FCSTD DOCUMENT  (FreeCAD 0.19R14555 (Git shallow))
Label: dfsdfd
License: All rights reserved
LicenseURL: http://en.wikipedia.org/wiki/All_rights_reserved
objects: Sketcher::SketchObject×1, PartDesign::Body×1
note: 2 computed .brp shape members not serialized (recipe doc carries the construction recipe); baked Part::Feature solids carry a one-line shape summary decoded from their .brp

FEATURE [Sketcher::SketchObject] Sketch
  FullyConstrained = false
  MapMode = 5
  Support = -> [XY_Plane]
  sketch-geometry (98):
    g0: LineSegment StartX=-62.5 StartY=60 StartZ=0 EndX=62.5 EndY=60 EndZ=0
    g1: LineSegment StartX=62.5 StartY=60 StartZ=0 EndX=62.5 EndY=0 EndZ=0
    g2: LineSegment StartX=62.5 StartY=0 StartZ=0 EndX=-62.5 EndY=0 EndZ=0
    g3: LineSegment StartX=-62.5 StartY=0 StartZ=0 EndX=-62.5 EndY=60 EndZ=0
    g4: LineSegment StartX=-82.5 StartY=25 StartZ=0 EndX=-127.5 EndY=25 EndZ=0
    g5: LineSegment StartX=-127.5 StartY=25 StartZ=0 EndX=-127.5 EndY=0 EndZ=0
    g6: LineSegment StartX=-127.5 StartY=0 StartZ=0 EndX=-82.5 EndY=0 EndZ=0
    g7: LineSegment StartX=-82.5 StartY=0 StartZ=0 EndX=-82.5 EndY=25 EndZ=0
    g8: LineSegment StartX=-147.5 StartY=25 StartZ=0 EndX=-192.5 EndY=25 EndZ=0
    g9: LineSegment StartX=-192.5 StartY=25 StartZ=0 EndX=-192.5 EndY=0 EndZ=0
    g10: LineSegment StartX=-192.5 StartY=0 StartZ=0 EndX=-147.5 EndY=0 EndZ=0
    g11: LineSegment StartX=-147.5 StartY=0 StartZ=0 EndX=-147.5 EndY=25 EndZ=0
    g12: LineSegment StartX=-62.5 StartY=35 StartZ=0 EndX=-200 EndY=35 EndZ=0
    g13: LineSegment StartX=-200 StartY=35 StartZ=0 EndX=-220.856 EndY=17.5 EndZ=0
    g14: LineSegment StartX=-220.856 StartY=17.5 StartZ=0 EndX=-200 EndY=0 EndZ=0
    g15: LineSegment StartX=-200 StartY=0 StartZ=0 EndX=-220.856 EndY=-17.5 EndZ=0
    g16: LineSegment StartX=-220.856 StartY=-17.5 StartZ=0 EndX=-200 EndY=-35 EndZ=0
    g17: LineSegment StartX=-200 StartY=-35 StartZ=0 EndX=0 EndY=-35 EndZ=0
    g18: LineSegment StartX=-192.5 StartY=-10 StartZ=0 EndX=-147.5 EndY=-10 EndZ=0
    g19: LineSegment StartX=-147.5 StartY=-10 StartZ=0 EndX=-147.5 EndY=-35 EndZ=0
    g20: LineSegment StartX=-147.5 StartY=-35 StartZ=0 EndX=-192.5 EndY=-35 EndZ=0
    g21: LineSegment StartX=-192.5 StartY=-35 StartZ=0 EndX=-192.5 EndY=-10 EndZ=0
    g22: LineSegment StartX=-127.5 StartY=-10 StartZ=0 EndX=-82.5 EndY=-10 EndZ=0
    g23: LineSegment StartX=-82.5 StartY=-10 StartZ=0 EndX=-82.5 EndY=-35 EndZ=0
    g24: LineSegment StartX=-82.5 StartY=-35 StartZ=0 EndX=-127.5 EndY=-35 EndZ=0
    g25: LineSegment StartX=-127.5 StartY=-35 StartZ=0 EndX=-127.5 EndY=-10 EndZ=0
    g26: LineSegment StartX=-192.5 StartY=60 StartZ=0 EndX=-147.5 EndY=60 EndZ=0
    g27: LineSegment StartX=-147.5 StartY=60 StartZ=0 EndX=-147.5 EndY=35 EndZ=0
    g28: LineSegment StartX=-147.5 StartY=35 StartZ=0 EndX=-192.5 EndY=35 EndZ=0
    g29: LineSegment StartX=-192.5 StartY=35 StartZ=0 EndX=-192.5 EndY=60 EndZ=0
    g30: LineSegment StartX=-127.5 StartY=60 StartZ=0 EndX=-82.5 EndY=60 EndZ=0
    g31: LineSegment StartX=-82.5 StartY=60 StartZ=0 EndX=-82.5 EndY=35 EndZ=0
    g32: LineSegment StartX=-82.5 StartY=35 StartZ=0 EndX=-127.5 EndY=35 EndZ=0
    g33: LineSegment StartX=-127.5 StartY=35 StartZ=0 EndX=-127.5 EndY=60 EndZ=0
    g34: LineSegment StartX=-4.5 StartY=12 StartZ=0 EndX=4.5 EndY=12 EndZ=0
    g35: LineSegment StartX=4.5 StartY=12 StartZ=0 EndX=4.5 EndY=0 EndZ=0
    g36: LineSegment StartX=4.5 StartY=0 StartZ=0 EndX=-4.5 EndY=0 EndZ=0
    g37: LineSegment StartX=-4.5 StartY=0 StartZ=0 EndX=-4.5 EndY=12 EndZ=0
    g38: LineSegment StartX=-4.5 StartY=-23 StartZ=0 EndX=4.5 EndY=-23 EndZ=0
    g39: LineSegment StartX=4.5 StartY=-23 StartZ=0 EndX=4.5 EndY=-35 EndZ=0
    g40: LineSegment StartX=4.5 StartY=-35 StartZ=0 EndX=-4.5 EndY=-35 EndZ=0
    g41: LineSegment StartX=-4.5 StartY=-35 StartZ=0 EndX=-4.5 EndY=-23 EndZ=0
    g42: LineSegment StartX=-62.5 StartY=-10 StartZ=0 EndX=-17.5 EndY=-10 EndZ=0
    g43: LineSegment StartX=-17.5 StartY=-10 StartZ=0 EndX=-17.5 EndY=-35 EndZ=0
    g44: LineSegment StartX=-17.5 StartY=-35 StartZ=0 EndX=-62.5 EndY=-35 EndZ=0
    g45: LineSegment StartX=-62.5 StartY=-35 StartZ=0 EndX=-62.5 EndY=-10 EndZ=0
    g46: LineSegment StartX=-200 StartY=0 StartZ=0 EndX=-62.5 EndY=0 EndZ=0
    g47: LineSegment StartX=-62.5 StartY=35 StartZ=0 EndX=62.5 EndY=35 EndZ=0
    g48: LineSegment StartX=-17.5 StartY=0 StartZ=0 EndX=-52.5 EndY=35 EndZ=0
    g49: LineSegment StartX=62.5 StartY=60 StartZ=0 EndX=-62.5 EndY=60 EndZ=0
    g50: LineSegment StartX=-62.5 StartY=60 StartZ=0 EndX=-62.5 EndY=0 EndZ=0
    g51: LineSegment StartX=-62.5 StartY=0 StartZ=0 EndX=62.5 EndY=0 EndZ=0
    g52: LineSegment StartX=62.5 StartY=0 StartZ=0 EndX=62.5 EndY=60 EndZ=0
    g53: LineSegment StartX=82.5 StartY=25 StartZ=0 EndX=127.5 EndY=25 EndZ=0
    g54: LineSegment StartX=127.5 StartY=25 StartZ=0 EndX=127.5 EndY=0 EndZ=0
    g55: LineSegment StartX=127.5 StartY=0 StartZ=0 EndX=82.5 EndY=0 EndZ=0
    g56: LineSegment StartX=82.5 StartY=0 StartZ=0 EndX=82.5 EndY=25 EndZ=0
    g57: LineSegment StartX=147.5 StartY=25 StartZ=0 EndX=192.5 EndY=25 EndZ=0
    g58: LineSegment StartX=192.5 StartY=25 StartZ=0 EndX=192.5 EndY=0 EndZ=0
    g59: LineSegment StartX=192.5 StartY=0 StartZ=0 EndX=147.5 EndY=0 EndZ=0
    g60: LineSegment StartX=147.5 StartY=0 StartZ=0 EndX=147.5 EndY=25 EndZ=0
    g61: LineSegment StartX=62.5 StartY=35 StartZ=0 EndX=200 EndY=35 EndZ=0
    g62: LineSegment StartX=200 StartY=35 StartZ=0 EndX=220.856 EndY=17.5 EndZ=0
    g63: LineSegment StartX=220.856 StartY=17.5 StartZ=0 EndX=200 EndY=0 EndZ=0
    g64: LineSegment StartX=200 StartY=0 StartZ=0 EndX=220.856 EndY=-17.5 EndZ=0
    g65: LineSegment StartX=220.856 StartY=-17.5 StartZ=0 EndX=200 EndY=-35 EndZ=0
    g66: LineSegment StartX=200 StartY=-35 StartZ=0 EndX=0 EndY=-35 EndZ=0
    g67: LineSegment StartX=192.5 StartY=-10 StartZ=0 EndX=147.5 EndY=-10 EndZ=0
    g68: LineSegment StartX=147.5 StartY=-10 StartZ=0 EndX=147.5 EndY=-35 EndZ=0
    g69: LineSegment StartX=147.5 StartY=-35 StartZ=0 EndX=192.5 EndY=-35 EndZ=0
    g70: LineSegment StartX=192.5 StartY=-35 StartZ=0 EndX=192.5 EndY=-10 EndZ=0
    g71: LineSegment StartX=127.5 StartY=-10 StartZ=0 EndX=82.5 EndY=-10 EndZ=0
    g72: LineSegment StartX=82.5 StartY=-10 StartZ=0 EndX=82.5 EndY=-35 EndZ=0
    g73: LineSegment StartX=82.5 StartY=-35 StartZ=0 EndX=127.5 EndY=-35 EndZ=0
    g74: LineSegment StartX=127.5 StartY=-35 StartZ=0 EndX=127.5 EndY=-10 EndZ=0
    g75: LineSegment StartX=192.5 StartY=60 StartZ=0 EndX=147.5 EndY=60 EndZ=0
    g76: LineSegment StartX=147.5 StartY=60 StartZ=0 EndX=147.5 EndY=35 EndZ=0
    g77: LineSegment StartX=147.5 StartY=35 StartZ=0 EndX=192.5 EndY=35 EndZ=0
    g78: LineSegment StartX=192.5 StartY=35 StartZ=0 EndX=192.5 EndY=60 EndZ=0
    g79: LineSegment StartX=127.5 StartY=60 StartZ=0 EndX=82.5 EndY=60 EndZ=0
    g80: LineSegment StartX=82.5 StartY=60 StartZ=0 EndX=82.5 EndY=35 EndZ=0
    g81: LineSegment StartX=82.5 StartY=35 StartZ=0 EndX=127.5 EndY=35 EndZ=0
    g82: LineSegment StartX=127.5 StartY=35 StartZ=0 EndX=127.5 EndY=60 EndZ=0
    g83: LineSegment StartX=4.5 StartY=12 StartZ=0 EndX=-4.5 EndY=12 EndZ=0
    g84: LineSegment StartX=-4.5 StartY=12 StartZ=0 EndX=-4.5 EndY=0 EndZ=0
    g85: LineSegment StartX=-4.5 StartY=0 StartZ=0 EndX=4.5 EndY=0 EndZ=0
    g86: LineSegment StartX=4.5 StartY=0 StartZ=0 EndX=4.5 EndY=12 EndZ=0
    g87: LineSegment StartX=4.5 StartY=-23 StartZ=0 EndX=-4.5 EndY=-23 EndZ=0
    g88: LineSegment StartX=-4.5 StartY=-23 StartZ=0 EndX=-4.5 EndY=-35 EndZ=0
    g89: LineSegment StartX=-4.5 StartY=-35 StartZ=0 EndX=4.5 EndY=-35 EndZ=0
    g90: LineSegment StartX=4.5 StartY=-35 StartZ=0 EndX=4.5 EndY=-23 EndZ=0
    g91: LineSegment StartX=62.5 StartY=-10 StartZ=0 EndX=17.5 EndY=-10 EndZ=0
    g92: LineSegment StartX=17.5 StartY=-10 StartZ=0 EndX=17.5 EndY=-35 EndZ=0
    g93: LineSegment StartX=17.5 StartY=-35 StartZ=0 EndX=62.5 EndY=-35 EndZ=0
    g94: LineSegment StartX=62.5 StartY=-35 StartZ=0 EndX=62.5 EndY=-10 EndZ=0
    g95: LineSegment StartX=200 StartY=0 StartZ=0 EndX=62.5 EndY=0 EndZ=0
    g96: LineSegment StartX=62.5 StartY=35 StartZ=0 EndX=-62.5 EndY=35 EndZ=0
    g97: LineSegment StartX=17.5 StartY=0 StartZ=0 EndX=52.5 EndY=35 EndZ=0
  constraints (279):
    c: Coincident(g0,g1)
    c: Coincident(g1,g2)
    c: Coincident(g2,g3)
    c: Coincident(g3,g0)
    c: Horizontal(g0)
    c: Horizontal(g2)
    c: Vertical(g1)
    c: Vertical(g3)
    c: PointOnObject(g1,g-1)
    c: Coincident(g4,g5)
    c: Coincident(g5,g6)
    c: Coincident(g6,g7)
    c: Coincident(g7,g4)
    c: Horizontal(g4)
    c: Horizontal(g6)
    c: Vertical(g5)
    c: Vertical(g7)
    c: Coincident(g8,g9)
    c: Coincident(g9,g10)
    c: Coincident(g10,g11)
    c: Coincident(g11,g8)
    c: Horizontal(g8)
    c: Horizontal(g10)
    c: Vertical(g9)
    c: Vertical(g11)
    c: PointOnObject(g9,g-1)
    c: Horizontal(g12)
    c: Coincident(g13,g12)
    c: Coincident(g14,g13)
    c: PointOnObject(g14,g-1)
    c: Coincident(g15,g14)
    c: Coincident(g16,g15)
    c: Coincident(g17,g16)
    c: PointOnObject(g17,g-2)
    c: Horizontal(g17)
    c: Coincident(g18,g19)
    c: Coincident(g19,g20)
    c: Coincident(g20,g21)
    c: Coincident(g21,g18)
    c: Horizontal(g18)
    c: Horizontal(g20)
    c: Vertical(g19)
    c: Vertical(g21)
    c: Coincident(g22,g23)
    c: Coincident(g23,g24)
    c: Coincident(g24,g25)
    c: Coincident(g25,g22)
    c: Horizontal(g22)
    c: Horizontal(g24)
    c: Vertical(g23)
    c: Vertical(g25)
    c: Coincident(g26,g27)
    c: Coincident(g27,g28)
    c: Coincident(g28,g29)
    c: Coincident(g29,g26)
    c: Horizontal(g26)
    c: Horizontal(g28)
    c: Vertical(g27)
    c: Vertical(g29)
    c: Coincident(g30,g31)
    c: Coincident(g31,g32)
    c: Coincident(g32,g33)
    c: Coincident(g33,g30)
    c: Horizontal(g30)
    c: Horizontal(g32)
    c: Vertical(g31)
    c: Vertical(g33)
    c: Coincident(g34,g35)
    c: Coincident(g35,g36)
    c: Coincident(g36,g37)
    c: Coincident(g37,g34)
    c: Horizontal(g34)
    c: Horizontal(g36)
    c: Vertical(g35)
    c: Vertical(g37)
    c: Coincident(g38,g39)
    c: Coincident(g39,g40)
    c: Coincident(g40,g41)
    c: Coincident(g41,g38)
    c: Horizontal(g38)
    c: Horizontal(g40)
    c: Vertical(g39)
    c: Vertical(g41)
    c: Coincident(g42,g43)
    c: Coincident(g43,g44)
    c: Coincident(g44,g45)
    c: Coincident(g45,g42)
    c: Horizontal(g42)
    c: Horizontal(g44)
    c: Vertical(g43)
    c: Vertical(g45)
    c: Coincident(g46,g14)
    c: Coincident(g46,g2)
    c: Equal(g13,g14)
    c: Equal(g15,g16)
    c: Equal(g15,g14)
    c: Equal(g37,g41)
    c: Equal(g36,g38)
    c: Equal(g27,g33)
    c: Equal(g33,g5)
    c: Equal(g5,g11)
    c: Equal(g11,g19)
    c: Equal(g19,g25)
    c: Equal(g25,g45)
    c: Equal(g42,g22)
    c: Equal(g22,g4)
    c: Equal(g4,g8)
    c: Equal(g8,g18)
    c: Equal(g18,g26)
    c: Equal(g26,g30)
    c: Angle(g17,g16) = 2.44346
    c: Angle(g46,g14) = 2.44346
    c: Angle(g15,g46) = 2.44346
    c: Angle(g13,g12) = 2.44346
    c: PointOnObject(g47,g3)
    c: PointOnObject(g47,g1)
    c: Horizontal(g47)
    c: PointOnObject(g48,g2)
    c: PointOnObject(g48,g47)
    c: Angle(g2,g48) = 2.35619
    c: DistanceX(g47,g48) = 10
    c: DistanceX(g0,g0) = 125
    c: DistanceY(g14,g12) = 35
    c: PointOnObject(g6,g46)
    c: PointOnObject(g23,g17)
    c: PointOnObject(g19,g17)
    c: PointOnObject(g44,g17)
    c: PointOnObject(g32,g12)
    c: PointOnObject(g27,g12)
    c: PointOnObject(g27,g11)
    c: PointOnObject(g10,g19)
    c: PointOnObject(g31,g7)
    c: PointOnObject(g22,g7)
    c: DistanceX(g26,g30) = 20
    c: DistanceX(g22,g42) = 20
    c: DistanceY(g3,g3) = 60
    c: PointOnObject(g36,g2)
    c: PointOnObject(g40,g17)
    c: DistanceY(g39,g39) = 12
    c: DistanceX(g38,g38) = 9
    c: DistanceX(g34,g-1) = 4.5
    c: DistanceX(g38,g-1) = 4.5
    c: DistanceX(g0,g-1) = 62.5
    c: DistanceX(g42,g42) = 45
    c: Coincident(g12,g47)
    c: DistanceX(g14,g-1) = 200
    c: PointOnObject(g30,g0)
    c: PointOnObject(g2,g45)
    c: Coincident(g49,g50)
    c: Coincident(g50,g51)
    c: Coincident(g51,g52)
    c: Coincident(g52,g49)
    c: Horizontal(g49)
    c: Horizontal(g51)
    c: Vertical(g50)
    c: Vertical(g52)
    c: Coincident(g53,g54)
    c: Coincident(g54,g55)
    c: Coincident(g55,g56)
    c: Coincident(g56,g53)
    c: Horizontal(g53)
    c: Horizontal(g55)
    c: Vertical(g54)
    c: Vertical(g56)
    c: Coincident(g57,g58)
    c: Coincident(g58,g59)
    c: Coincident(g59,g60)
    c: Coincident(g60,g57)
    c: Horizontal(g57)
    c: Horizontal(g59)
    c: Vertical(g58)
    c: Vertical(g60)
    c: Horizontal(g61)
    c: Coincident(g62,g61)
    c: Coincident(g63,g62)
    c: Coincident(g64,g63)
    c: Coincident(g65,g64)
    c: Coincident(g66,g65)
    c: Horizontal(g66)
    c: Coincident(g67,g68)
    c: Coincident(g68,g69)
    c: Coincident(g69,g70)
    c: Coincident(g70,g67)
    c: Horizontal(g67)
    c: Horizontal(g69)
    c: Vertical(g68)
    c: Vertical(g70)
    c: Coincident(g71,g72)
    c: Coincident(g72,g73)
    c: Coincident(g73,g74)
    c: Coincident(g74,g71)
    c: Horizontal(g71)
    c: Horizontal(g73)
    c: Vertical(g72)
    c: Vertical(g74)
    c: Coincident(g75,g76)
    c: Coincident(g76,g77)
    c: Coincident(g77,g78)
    c: Coincident(g78,g75)
    c: Horizontal(g75)
    c: Horizontal(g77)
    c: Vertical(g76)
    c: Vertical(g78)
    c: Coincident(g79,g80)
    c: Coincident(g80,g81)
    c: Coincident(g81,g82)
    c: Coincident(g82,g79)
    c: Horizontal(g79)
    c: Horizontal(g81)
    c: Vertical(g80)
    c: Vertical(g82)
    c: Coincident(g83,g84)
    c: Coincident(g84,g85)
    c: Coincident(g85,g86)
    c: Coincident(g86,g83)
    c: Horizontal(g83)
    c: Horizontal(g85)
    c: Vertical(g84)
    c: Vertical(g86)
    c: Coincident(g87,g88)
    c: Coincident(g88,g89)
    c: Coincident(g89,g90)
    c: Coincident(g90,g87)
    c: Horizontal(g87)
    c: Horizontal(g89)
    c: Vertical(g88)
    c: Vertical(g90)
    c: Coincident(g91,g92)
    c: Coincident(g92,g93)
    c: Coincident(g93,g94)
    c: Coincident(g94,g91)
    c: Horizontal(g91)
    c: Horizontal(g93)
    c: Vertical(g92)
    c: Vertical(g94)
    c: Coincident(g95,g63)
    c: Coincident(g95,g51)
    c: Equal(g62,g63)
    c: Equal(g64,g65)
    c: Equal(g64,g63)
    c: Equal(g86,g90)
    c: Equal(g85,g87)
    c: Equal(g76,g82)
    c: Equal(g82,g54)
    c: Equal(g54,g60)
    c: Equal(g60,g68)
    c: Equal(g68,g74)
    c: Equal(g74,g94)
    c: Equal(g91,g71)
    c: Equal(g71,g53)
    c: Equal(g53,g57)
    c: Equal(g57,g67)
    c: Equal(g67,g75)
    c: Equal(g75,g79)
    c: Angle(g66,g65) = -2.44346
    c: Angle(g95,g63) = -2.44346
    c: Angle(g64,g95) = -2.44346
    c: Angle(g62,g61) = -2.44346
    c: PointOnObject(g96,g52)
    c: PointOnObject(g96,g50)
    c: Horizontal(g96)
    c: PointOnObject(g97,g51)
    c: PointOnObject(g97,g96)
    c: Angle(g51,g97) = -2.35619
    c: PointOnObject(g55,g95)
    c: PointOnObject(g72,g66)
    c: PointOnObject(g68,g66)
    c: PointOnObject(g93,g66)
    c: PointOnObject(g81,g61)
    c: PointOnObject(g76,g61)
    c: PointOnObject(g76,g60)
    c: PointOnObject(g59,g68)
    c: PointOnObject(g80,g56)
    c: PointOnObject(g71,g56)
    c: PointOnObject(g85,g51)
    c: PointOnObject(g89,g66)
    c: Coincident(g61,g96)
    c: PointOnObject(g79,g49)
    c: PointOnObject(g51,g94)
FEATURE [PartDesign::Body] Body
  Group = -> [Sketch]
  Origin = -> Origin
